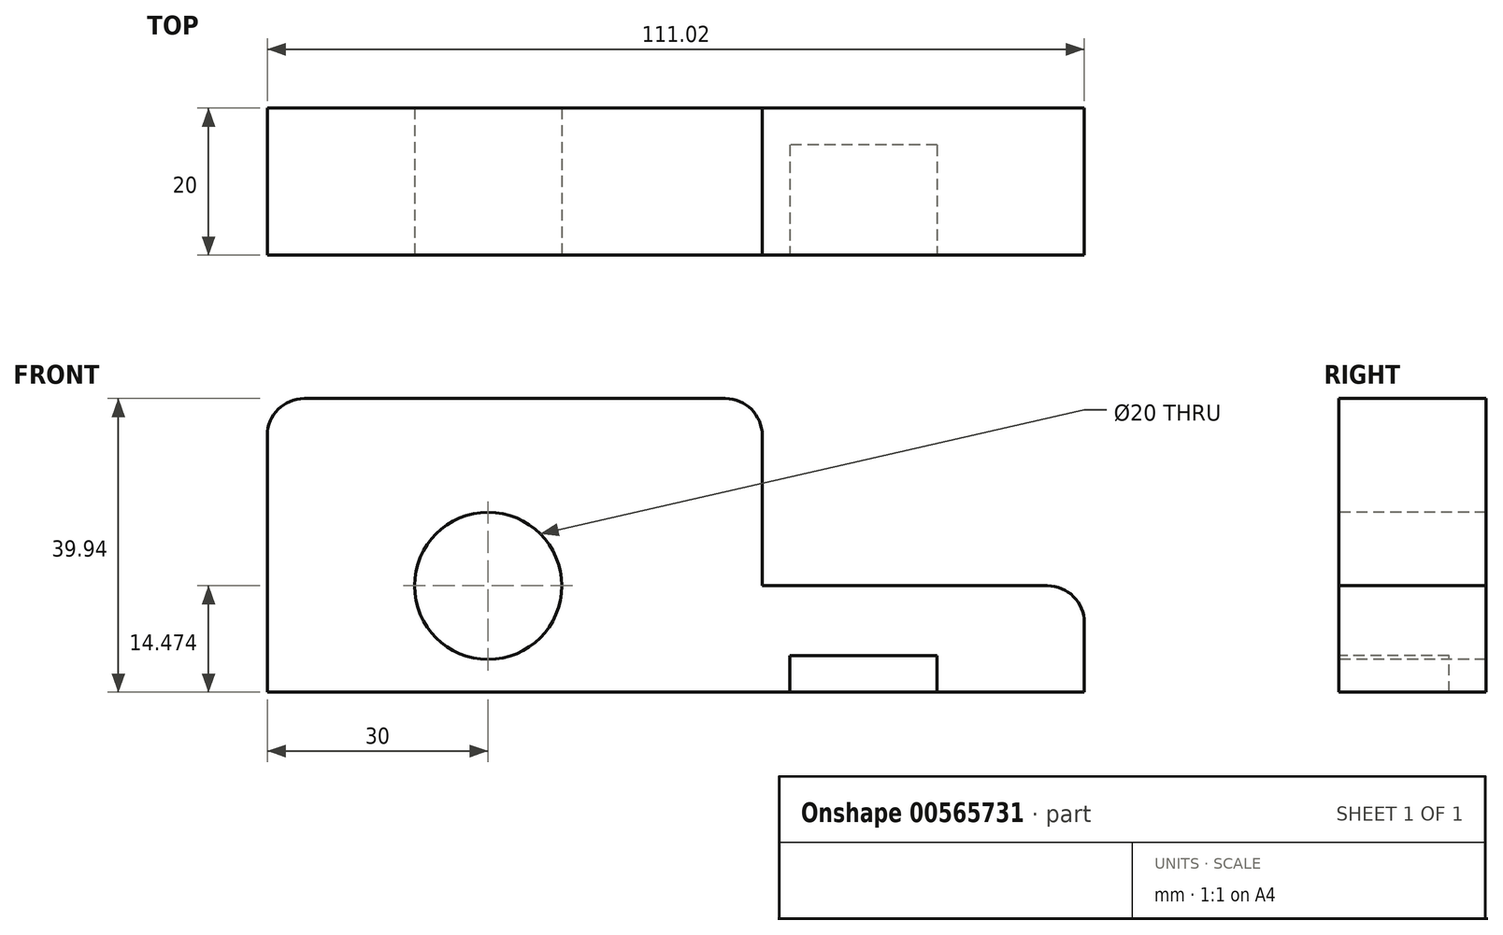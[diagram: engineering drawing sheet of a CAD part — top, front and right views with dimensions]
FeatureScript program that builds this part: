
annotation { "Feature Type Name" : "Feature", "Feature Type Description" : "" }
export const myFeature = defineFeature(function(context is Context, id is Id, definition is map)
    precondition{}
    {
        {
            var Q0;
            Q0=qCreatedBy(makeId("Front.planeOp"),FACE);
            var sketch = newSketch(context, id + "F0", { "sketchPlane" : qUnion([Q0])});
            skLineSegment(sketch, "E0", {"start": v(0, 0) * mm, "end": v(0, 39.94) * mm});
            skLineSegment(sketch, "E1", {"start": v(0, 39.94) * mm, "end": v(67.25, 39.94) * mm});
            skLineSegment(sketch, "E2", {"start": v(67.25, 39.94) * mm, "end": v(67.25, 14.47) * mm});
            skLineSegment(sketch, "E3", {"start": v(67.25, 14.47) * mm, "end": v(111.02, 14.47) * mm});
            skLineSegment(sketch, "E4", {"start": v(111.02, 14.47) * mm, "end": v(111.02, 0) * mm});
            skLineSegment(sketch, "E5", {"start": v(111.02, 0) * mm, "end": v(0, 0) * mm});
            skSolve(sketch);
        }
        {
            var Q0;
            Q0 = qSketchRegion(id + "F0", true);
            extrude(context, id + "F1", {"entities" : qUnion([Q0]), "depth" : 20 * mm, "offsetDistance" : 25 * mm});
        }
        {
            var Q0;
            Q0=makeQuery(id+"F1.opExtrude","SWEPT_EDGE",EDGE,{"disambiguationData":[OSD([sQuery(id+"F0.wireOp",EDGE,"E1"),sQuery(id+"F0.wireOp",EDGE,"E2")])]});
            var Q1;
            Q1=makeQuery(id+"F1.opExtrude","SWEPT_EDGE",EDGE,{"disambiguationData":[OSD([sQuery(id+"F0.wireOp",EDGE,"E3"),sQuery(id+"F0.wireOp",EDGE,"E4")])]});
            var Q2;
            Q2=makeQuery(id+"F1.opExtrude","SWEPT_EDGE",EDGE,{"disambiguationData":[OSD([sQuery(id+"F0.wireOp",EDGE,"E0"),sQuery(id+"F0.wireOp",EDGE,"E1")])]});
            fillet(context, id + "F2", {"entities" : qUnion([Q0, Q1, Q2]), "radius" : 5 * mm, "tangentPropagation" : true, "allowEdgeOverflow" : false});
        }
        {
            var Q0;
            Q0=makeQuery(id+"F1.opExtrude","CAP_FACE",FACE,{"disambiguationData":[OSD([sQuery(id+"F0.wireOp",EDGE,"E0"),sQuery(id+"F0.wireOp",EDGE,"E1"),sQuery(id+"F0.wireOp",EDGE,"E2"),sQuery(id+"F0.wireOp",EDGE,"E3"),sQuery(id+"F0.wireOp",EDGE,"E4"),sQuery(id+"F0.wireOp",EDGE,"E5")])],"isStart":false});
            var sketch = newSketch(context, id + "F3", { "sketchPlane" : qUnion([Q0])});
            skCircle(sketch, "E6", {"center": v(30, 14.47) * mm, "radius": 10 * mm});
            skSolve(sketch);
        }
        {
            var Q0;
            Q0=makeQuery(id+"F3.imprint","IMPRINT",FACE,{"disambiguationData":[TD([[makeQuery(id+"F3.imprint","IMPRINT",EDGE,{"derivedFrom":sQuery(id+"F3.wireOp",EDGE,"E6")}),1.0]])]});
            extrude(context, id + "F4", {"entities" : qUnion([Q0]), "operationType" : NewBodyOperationType.REMOVE, "endBound" : BoundingType.THROUGH_ALL, "oppositeDirection" : true, "depth" : 25 * mm, "offsetDistance" : 25 * mm});
        }
        {
            var Q0;
            Q0=makeQuery(id+"F1.opExtrude","CAP_FACE",FACE,{"disambiguationData":[OSD([sQuery(id+"F0.wireOp",EDGE,"E0"),sQuery(id+"F0.wireOp",EDGE,"E1"),sQuery(id+"F0.wireOp",EDGE,"E2"),sQuery(id+"F0.wireOp",EDGE,"E3"),sQuery(id+"F0.wireOp",EDGE,"E4"),sQuery(id+"F0.wireOp",EDGE,"E5")])],"isStart":false});
            var sketch = newSketch(context, id + "F5", { "sketchPlane" : qUnion([Q0])});
            skLineSegment(sketch, "E7.bottom", {"start": v(71.02, 0) * mm, "end": v(91.02, 0) * mm});
            skLineSegment(sketch, "E7.top", {"start": v(71.02, 5) * mm, "end": v(91.02, 5) * mm});
            skLineSegment(sketch, "E7.left", {"start": v(71.02, 0) * mm, "end": v(71.02, 5) * mm});
            skLineSegment(sketch, "E7.right", {"start": v(91.02, 0) * mm, "end": v(91.02, 5) * mm});
            skSolve(sketch);
        }
        {
            var Q0;
            Q0=makeQuery(id+"F5.imprint","IMPRINT",FACE,{"disambiguationData":[TD([[makeQuery(id+"F5.imprint","IMPRINT",EDGE,{"derivedFrom":sQuery(id+"F5.wireOp",EDGE,"E7.bottom")}),-1.0]])]});
            extrude(context, id + "F6", {"entities" : qUnion([Q0]), "operationType" : NewBodyOperationType.REMOVE, "oppositeDirection" : true, "depth" : 15 * mm, "offsetDistance" : 25 * mm});
        }
    });
